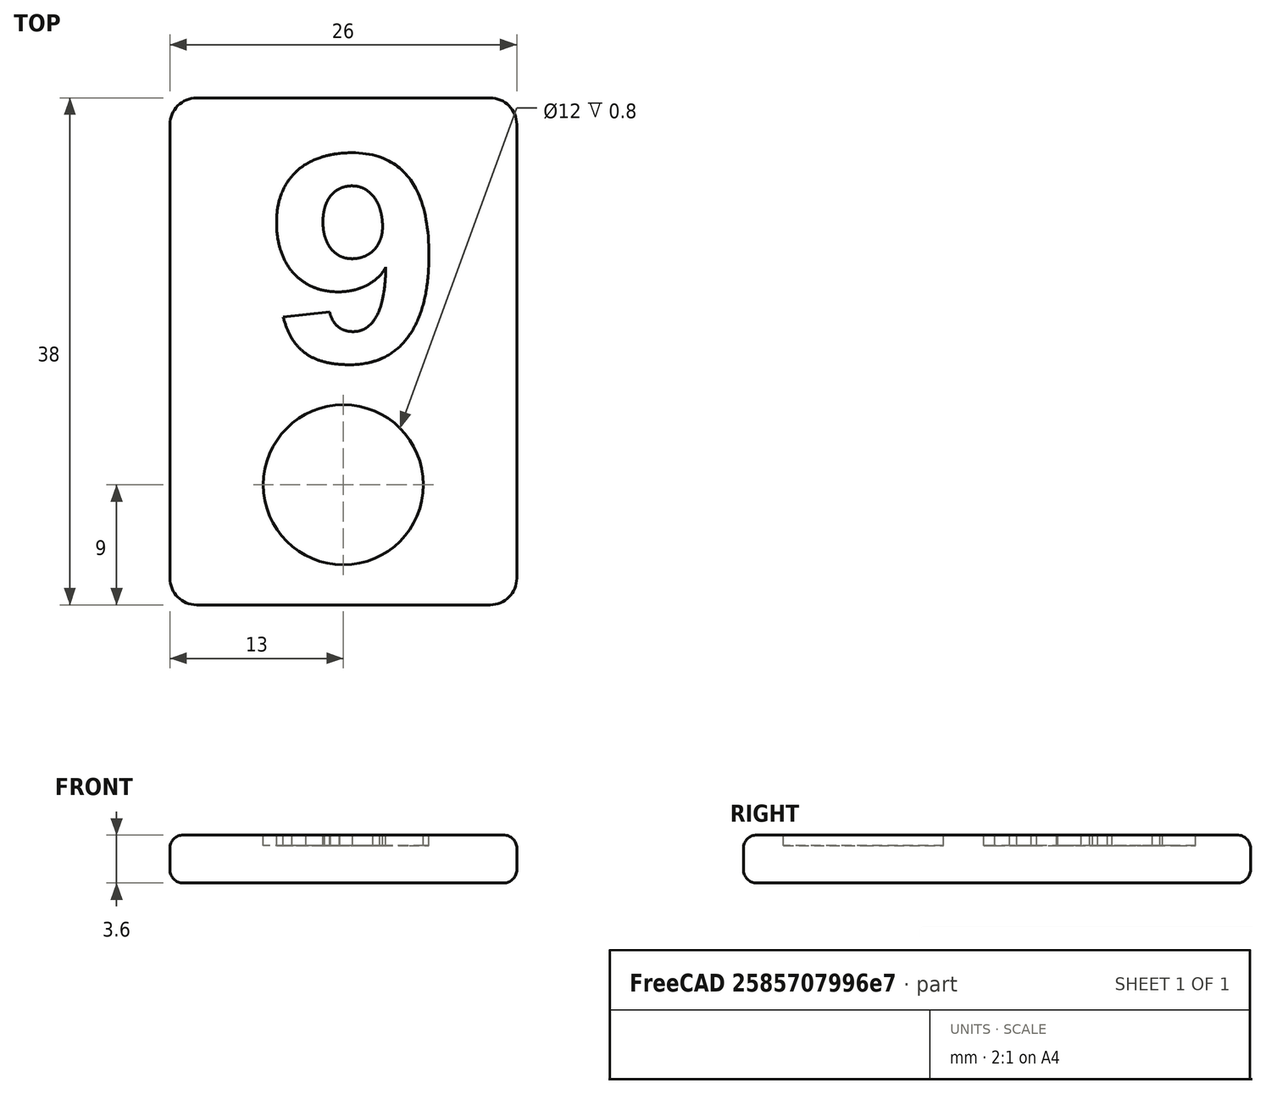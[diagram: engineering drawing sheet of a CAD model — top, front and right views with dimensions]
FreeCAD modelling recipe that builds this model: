
FCSTD DOCUMENT  (FreeCAD 0.14R3702 (Git))
Label: ficha9
License: CC-BY 3.0
LicenseURL: http://creativecommons.org/licenses/by/3.0/
objects: Part::Fillet×2, Part::Cut×2, Part::Box×1, Part::Part2DObjectPython×1, Part::Cylinder×1, Part::Extrusion×1
note: 8 computed .brp shape members not serialized (recipe doc carries the construction recipe); baked Part::Feature solids carry a one-line shape summary decoded from their .brp

FEATURE [Part::Box] Box  label="Cubo"
  Height = 3.6
  Length = 26
  Width = 38
FEATURE [Part::Fillet] Fillet
  Base = -> Box
  Edges = 4 edges r=2: [Edge1,Edge3,Edge5,Edge7]
FEATURE [Part::Part2DObjectPython] ShapeString  # Draft 2D object (typed FeaturePython)
  FontFile = <path>
  Placement = pos=(6.5,18,4) rot=(0,0,1;0rad)
  Size = 18
  String = 9
  Tracking = 0
FEATURE [Part::Cylinder] Cylinder  label="Cilindro"
  Angle = 360
  Height = 10
  Placement = pos=(13,9,2.8) rot=(0,0,1;0rad)
  Radius = 6
FEATURE [Part::Extrusion] Extrude001
  Base = -> ShapeString
  Dir = (0,0,2)
  Placement = pos=(0,0,-1.2) rot=(0,0,1;0rad)
  Solid = true
FEATURE [Part::Cut] Cut
  Base = -> Fillet
  Tool = -> Cylinder
FEATURE [Part::Cut] Cut001
  Base = -> Cut
  Tool = -> Extrude001
FEATURE [Part::Fillet] Fillet001
  Base = -> Cut001
  Edges = 16 edges r=1: [Edge1,Edge4,Edge34,Edge35,Edge36,Edge37,Edge38,Edge39,Edge40,Edge41,Edge43,Edge45,Edge46,Edge47,Edge48,Edge49]
note: 1 file-system path scrubbed to <path> (originals preserved in the JSON sidecar)
